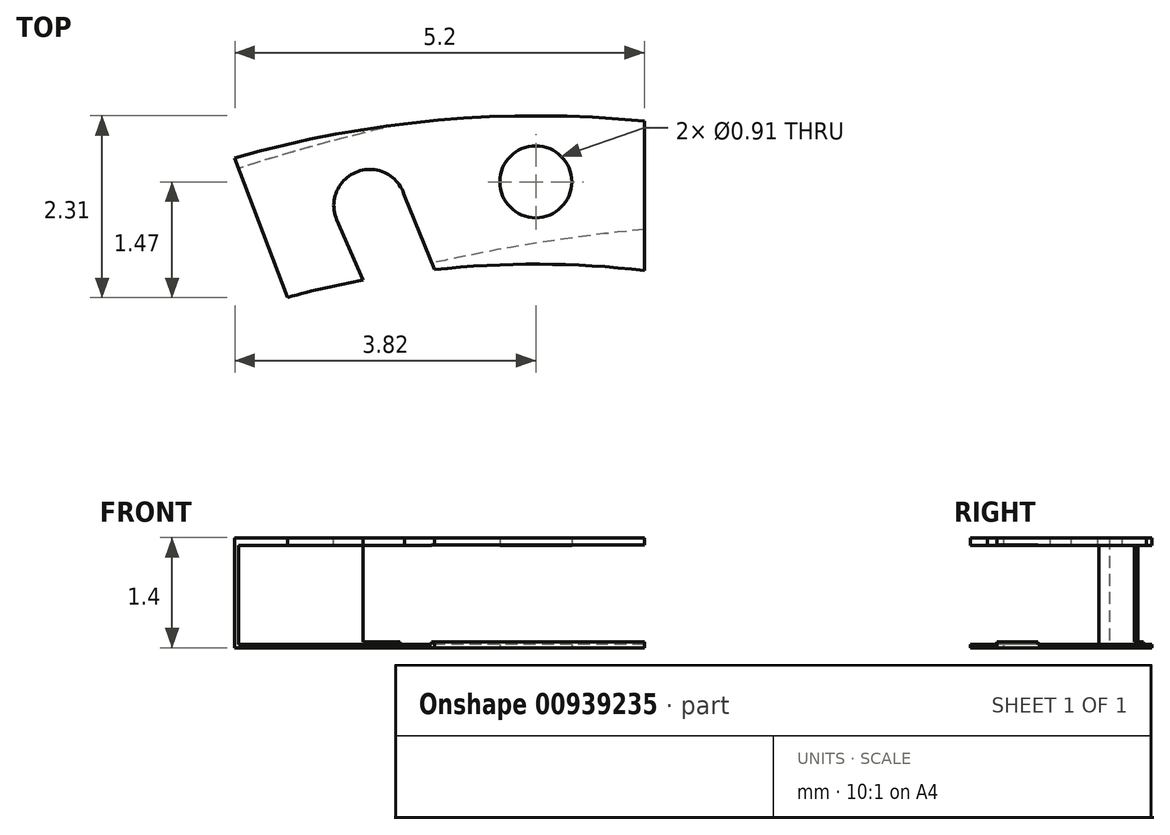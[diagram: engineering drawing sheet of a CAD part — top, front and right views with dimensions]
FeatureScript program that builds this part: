
annotation { "Feature Type Name" : "Feature", "Feature Type Description" : "" }
export const myFeature = defineFeature(function(context is Context, id is Id, definition is map)
    precondition{}
    {
        {
            var Q0;
            Q0=qCreatedBy(makeId("Front.planeOp"),FACE);
            cPlane(context, id + "F0", {"entities" : qUnion([Q0]), "cplaneType" : CPlaneType.OFFSET, "offset" : 13.92 * mm, "width" : 152.4 * mm, "height" : 152.4 * mm});
        }
        {
            var Q0;
            Q0=qCreatedBy(makeId("Top.planeOp"),FACE);
            var sketch = newSketch(context, id + "F1", { "sketchPlane" : qUnion([Q0])});
            skCircle(sketch, "E0", {"center": v(0, 0) * mm, "radius": 0.46 * mm});
            skArc(sketch, "E1", {"start": v(1.38, 0.77) * mm, "mid": v(-3.03, 0.5) * mm, "end": v(-7.13, -1.13) * mm});
            skArc(sketch, "E2", {"start": v(1.38, -1.13) * mm, "mid": v(-2.59, -1.33) * mm, "end": v(-6.28, -2.81) * mm});
            skLineSegment(sketch, "E3", {"start": v(-7.13, -1.13) * mm, "end": v(-6.28, -2.81) * mm});
            skLineSegment(sketch, "E4", {"start": v(1.38, -1.13) * mm, "end": v(1.38, 0.77) * mm});
            skCircle(sketch, "E5", {"center": v(0, -13.08) * mm, "radius": 13.72 * mm, "construction": true});
            skSolve(sketch);
        }
        {
            var Q0;
            Q0=makeQuery(id+"F1.imprint","IMPRINT",FACE,{"disambiguationData":[TD([[makeQuery(id+"F1.imprint","IMPRINT",EDGE,{"derivedFrom":sQuery(id+"F1.wireOp",EDGE,"E0")}),-1.0]])]});
            extrude(context, id + "F2", {"entities" : qUnion([Q0]), "depth" : 1.4 * mm, "offsetDistance" : 25.4 * mm});
        }
        {
            var Q0;
            Q0=makeQuery(id+"F2.opExtrude","SWEPT_FACE",FACE,{"disambiguationData":[OSD([sQuery(id+"F1.wireOp",EDGE,"E3")])]});
            var sketch = newSketch(context, id + "F3", { "sketchPlane" : qUnion([Q0])});
            skLineSegment(sketch, "E6.bottom", {"start": v(-0.32, 1.3) * mm, "end": v(-0.32, 1.3) * mm});
            skLineSegment(sketch, "E6.top", {"start": v(-0.32, 0.04) * mm, "end": v(-0.32, 0.04) * mm});
            skLineSegment(sketch, "E6.left", {"start": v(-0.32, 1.3) * mm, "end": v(-0.32, 0.04) * mm});
            skLineSegment(sketch, "E6.right", {"start": v(-0.32, 1.3) * mm, "end": v(-0.32, 0.04) * mm});
            skLineSegment(sketch, "E7.bottom", {"start": v(-0.32, 1.3) * mm, "end": v(-2.13, 1.3) * mm});
            skLineSegment(sketch, "E7.top", {"start": v(-0.32, 0.04) * mm, "end": v(-2.13, 0.04) * mm});
            skLineSegment(sketch, "E7.right", {"start": v(-2.13, 1.3) * mm, "end": v(-2.13, 0.04) * mm});
            skLineSegment(sketch, "E8.left", {"start": v(-2.13, 0.04) * mm, "end": v(-1.69, 0.04) * mm});
            skLineSegment(sketch, "E9", {"start": v(21.04, 0) * mm, "end": v(21.04, 12.93) * mm, "construction": true});
            skSolve(sketch);
        }
        {
            var Q0;
            Q0 = qSketchRegion(id + "F3", true);
            var Q1;
            Q1=sQuery(id+"F3.wireOp",EDGE,"E9");
            revolve(context, id + "F4", {"operationType" : NewBodyOperationType.REMOVE, "surfaceOperationType" : NewSurfaceOperationType.NEW, "entities" : qUnion([Q0]), "axis" : qUnion([Q1]), "revolveType" : RevolveType.FULL, "oppositeDirection" : true});
        }
        {
            var Q0;
            Q0=qCreatedBy(id+"F0.planeOp",FACE);
            var sketch = newSketch(context, id + "F5", { "sketchPlane" : qUnion([Q0])});
            skLineSegment(sketch, "E10.bottom", {"start": v(-2.18, 1.31) * mm, "end": v(1.41, 1.31) * mm});
            skLineSegment(sketch, "E10.top", {"start": v(-2.18, 0.06) * mm, "end": v(1.41, 0.06) * mm});
            skLineSegment(sketch, "E10.left", {"start": v(-2.18, 1.31) * mm, "end": v(-2.18, 0.06) * mm});
            skLineSegment(sketch, "E10.right", {"start": v(1.41, 1.31) * mm, "end": v(1.41, 0.06) * mm});
            skSolve(sketch);
        }
        {
            var Q0;
            Q0=makeQuery(id+"F5.imprint","IMPRINT",FACE,{"disambiguationData":[TD([[makeQuery(id+"F5.imprint","IMPRINT",EDGE,{"derivedFrom":sQuery(id+"F5.wireOp",EDGE,"E10.bottom")}),-1.0]])]});
            var sketch = newSketch(context, id + "F6", { "sketchPlane" : qUnion([Q0])});
            skLineSegment(sketch, "E11.bottom", {"start": v(-2.2, 1.3) * mm, "end": v(1.42, 1.3) * mm});
            skLineSegment(sketch, "E11.top", {"start": v(-2.2, 0.08) * mm, "end": v(1.42, 0.08) * mm});
            skLineSegment(sketch, "E11.left", {"start": v(-2.2, 1.3) * mm, "end": v(-2.2, 0.08) * mm});
            skLineSegment(sketch, "E11.right", {"start": v(1.42, 1.3) * mm, "end": v(1.42, 0.08) * mm});
            skSolve(sketch);
        }
        {
            var Q0;
            Q0 = qSketchRegion(id + "F6", true);
            extrude(context, id + "F7", {"entities" : qUnion([Q0]), "operationType" : NewBodyOperationType.REMOVE, "oppositeDirection" : true, "depth" : 25.4 * mm, "offsetDistance" : 25.4 * mm});
        }
        {
            var Q0;
            Q0=makeQuery(id+"F2.opExtrude","CAP_FACE",FACE,{"disambiguationData":[OSD([sQuery(id+"F1.wireOp",EDGE,"E0"),sQuery(id+"F1.wireOp",EDGE,"E1"),sQuery(id+"F1.wireOp",EDGE,"E2"),sQuery(id+"F1.wireOp",EDGE,"E3"),sQuery(id+"F1.wireOp",EDGE,"E4")])],"isStart":false});
            var sketch = newSketch(context, id + "F8", { "sketchPlane" : qUnion([Q0])});
            skArc(sketch, "E12", {"start": v(-1.67, -0.18) * mm, "mid": v(-2.26, 0.13) * mm, "end": v(-2.53, -0.48) * mm});
            skLineSegment(sketch, "E13", {"start": v(-2.53, -0.48) * mm, "end": v(-2.2, -1.25) * mm});
            skLineSegment(sketch, "E14", {"start": v(-1.67, -0.18) * mm, "end": v(-1.29, -1.12) * mm});
            skLineSegment(sketch, "E15", {"start": v(-1.29, -1.12) * mm, "end": v(-2.2, -1.25) * mm});
            skSolve(sketch);
        }
        {
            var Q0;
            Q0=makeQuery(id+"F8.imprint","IMPRINT",FACE,{"disambiguationData":[TD([[makeQuery(id+"F8.imprint","IMPRINT",EDGE,{"derivedFrom":sQuery(id+"F8.wireOp",EDGE,"E12")}),1.0]])]});
            extrude(context, id + "F9", {"entities" : qUnion([Q0]), "operationType" : NewBodyOperationType.REMOVE, "oppositeDirection" : true, "depth" : 25.4 * mm, "offsetDistance" : 25.4 * mm});
        }
        {
            var Q0;
            Q0=makeQuery(id+"F2.opExtrude","CAP_FACE",FACE,{"disambiguationData":[OSD([sQuery(id+"F1.wireOp",EDGE,"E0"),sQuery(id+"F1.wireOp",EDGE,"E1"),sQuery(id+"F1.wireOp",EDGE,"E2"),sQuery(id+"F1.wireOp",EDGE,"E3"),sQuery(id+"F1.wireOp",EDGE,"E4")])],"isStart":false});
            var sketch = newSketch(context, id + "F10", { "sketchPlane" : qUnion([Q0])});
            skLineSegment(sketch, "E16", {"start": v(-4, 0.77) * mm, "end": v(-2.74, -2.56) * mm});
            skLineSegment(sketch, "E17", {"start": v(-2.74, -2.56) * mm, "end": v(-6.45, -4.34) * mm});
            skLineSegment(sketch, "E18", {"start": v(-6.45, -4.34) * mm, "end": v(-7.9, -0.67) * mm});
            skLineSegment(sketch, "E19", {"start": v(-7.9, -0.67) * mm, "end": v(-4, 0.77) * mm});
            skSolve(sketch);
        }
        {
            var Q0;
            Q0 = qSketchRegion(id + "F10", true);
            extrude(context, id + "F11", {"entities" : qUnion([Q0]), "operationType" : NewBodyOperationType.REMOVE, "oppositeDirection" : true, "depth" : 25.4 * mm, "offsetDistance" : 25.4 * mm});
        }
    });
